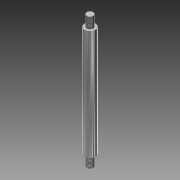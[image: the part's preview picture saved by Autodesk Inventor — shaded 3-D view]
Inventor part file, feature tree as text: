
AUTODESK INVENTOR PART (.ipt)
format: ipt  version: 2015 (Build 190159000, 159)  size: 82,432 bytes
history: native  units: mm
features: extrude x3, sketch x3, thread x2
ambient origin geometry x8: Origin, YZ Plane, XZ Plane, XY Plane, X Axis, Y Axis, Z Axis, Center Point
bodies: Solid1 (feature_tree)
feature tree (8):
  extrude  "Extrusion1"  Depth=50.0mm TaperAngle=0.0deg
  extrude  "Extrusion2"  Depth=5.0mm TaperAngle=0.0deg
  thread  "Thread1"  [1 undecoded]
  extrude  "Extrusion3"  Depth=5.0mm TaperAngle=0.0deg
  thread  "Thread2"  [1 undecoded]
  sketch  "Sketch1"  dims[d0=5.0mm d1=50.0mm d2=0.0mm]
  sketch  "Sketch2"  dims[d3=3.0mm d4=5.0mm d5=0.0mm d6=10.0mm d7=0.0mm]
  sketch  "Sketch3"  dims[d8=3.0mm d9=5.0mm d10=0.0mm d11=10.0mm d12=0.0mm]
note: 2 required parameter values undecoded (feature->parameter linkage not recoverable at this tier; creation-order binding heuristic only, values carry confidence <= 0.55)
